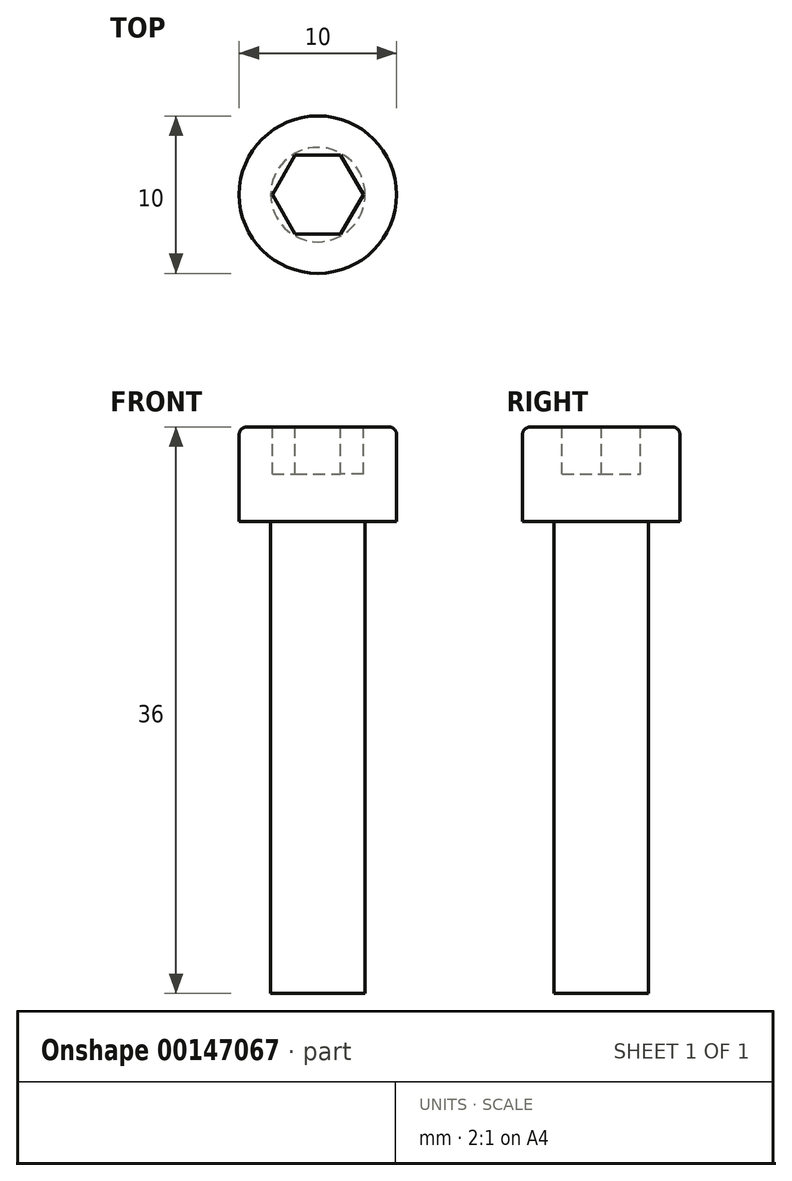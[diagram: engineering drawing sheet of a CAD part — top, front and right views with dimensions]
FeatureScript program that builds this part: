
annotation { "Feature Type Name" : "Feature", "Feature Type Description" : "" }
export const myFeature = defineFeature(function(context is Context, id is Id, definition is map)
    precondition{}
    {
        {
            var Q0;
            Q0=qCreatedBy(makeId("Front.planeOp"),FACE);
            var sketch = newSketch(context, id + "F0", { "sketchPlane" : qUnion([Q0])});
            skLineSegment(sketch, "E0", {"start": v(0, -30) * mm, "end": v(-3, -30) * mm});
            skLineSegment(sketch, "E1", {"start": v(-3, -30) * mm, "end": v(-3, 0) * mm});
            skLineSegment(sketch, "E2", {"start": v(-3, 0) * mm, "end": v(-5, 0) * mm});
            skLineSegment(sketch, "E3", {"start": v(-5, 0) * mm, "end": v(-5, 6) * mm});
            skLineSegment(sketch, "E4", {"start": v(-5, 6) * mm, "end": v(0, 6) * mm});
            skLineSegment(sketch, "E5", {"start": v(0, 6) * mm, "end": v(0, -30) * mm});
            skSolve(sketch);
        }
        {
            var Q0;
            Q0=makeQuery(id+"F0.imprint","IMPRINT",FACE,{"disambiguationData":[TD([[makeQuery(id+"F0.imprint","IMPRINT",EDGE,{"derivedFrom":sQuery(id+"F0.wireOp",EDGE,"E0")}),-1.0]])]});
            var Q1;
            Q1=sQuery(id+"F0.wireOp",EDGE,"E5");
            revolve(context, id + "F1", {"entities" : qUnion([Q0]), "axis" : qUnion([Q1]), "revolveType" : RevolveType.FULL});
        }
        {
            var Q0;
            Q0=makeQuery(id+"F1.opRevolve","SWEPT_FACE",FACE,{"disambiguationData":[OSD([sQuery(id+"F0.wireOp",EDGE,"E4")])]});
            var sketch = newSketch(context, id + "F2", { "sketchPlane" : qUnion([Q0])});
            skCircle(sketch, "E6.cCircle", {"center": v(0, 0) * mm, "radius": 2.5 * mm, "construction": true});
            skLineSegment(sketch, "E6.0", {"start": v(-1.44, 2.5) * mm, "end": v(1.44, 2.5) * mm});
            skLineSegment(sketch, "E6.1", {"start": v(1.44, 2.5) * mm, "end": v(2.89, 0) * mm});
            skLineSegment(sketch, "E6.2", {"start": v(2.89, 0) * mm, "end": v(1.44, -2.5) * mm});
            skLineSegment(sketch, "E6.3", {"start": v(1.44, -2.5) * mm, "end": v(-1.44, -2.5) * mm});
            skLineSegment(sketch, "E6.4", {"start": v(-1.44, -2.5) * mm, "end": v(-2.89, 0) * mm});
            skLineSegment(sketch, "E6.5", {"start": v(-2.89, 0) * mm, "end": v(-1.44, 2.5) * mm});
            skPoint(sketch, "E6.0.midPoint", {"position": v(0, 2.5) * mm});
            skSolve(sketch);
        }
        {
            var Q0;
            Q0 = qSketchRegion(id + "F2", true);
            extrude(context, id + "F3", {"entities" : qUnion([Q0]), "operationType" : NewBodyOperationType.REMOVE, "oppositeDirection" : true, "depth" : 3 * mm});
        }
        {
            var Q0;
            Q0=makeQuery(id+"F1.opRevolve","SWEPT_EDGE",EDGE,{"disambiguationData":[OSD([sQuery(id+"F0.wireOp",EDGE,"E3"),sQuery(id+"F0.wireOp",EDGE,"E4")])]});
            fillet(context, id + "F4", {"entities" : qUnion([Q0]), "radius" : .5 * mm, "tangentPropagation" : true, "allowEdgeOverflow" : false});
        }
    });
